# Revit family: Reece_Bath_LAUFEN_Val_Freestanding Bath_1300 mm_Round
name_source: partatom
category: Plumbing Fixtures
revit_build: Autodesk Revit 2018 (Build: 20180329_1100(x64)
units: mm (PartAtom-declared; Revit-internal decimal feet)

## family parameters
Always vertical = Yes
Cut with Voids When Loaded = Yes
Part Type = Normal
Room Calculation Point = Yes
Round Connector Dimension = Use Diameter
Shared = Yes
Work Plane-Based = Yes

## types (1)
- White
    Default Elevation = 0 mm  [stored 0 ft]
    Description = Laufen Val Freestanding Bath with Overflow 1300 Round Sentec White
    Disclaimer = THIS FILE IS THE PROPERTY OF THE REECE GROUP. IT MAY NOT BE REPRODUCED, REVERSE-ENGINEERED OR MODIFIED. ANY REPUBLICATION, TRANSMISSION OR DISTRIBUTION FOR THE PURPOSE OF COMMERCIALLY EXPLOITING THE FILES IS PROHIBITED.
    Keynote = Product #9510105, Reece_Bath_LAUFEN_Val_Freestanding Bath_1300 mm_Round - White
    Manufacturer = Laufen
    Model = Val
    Reece_Bath_Outlet = 40 mm  [stored 0.131234 ft]
    Reece_Detail_Additional = Overflow
    Reece_Detail_Disclaimer = THIS FILE IS THE PROPERTY OF THE REECE GROUP. IT MAY NOT BE REPRODUCED, REVERSE-ENGINEERED OR MODIFIED. ANY REPUBLICATION, TRANSMISSION OR DISTRIBUTION FOR THE PURPOSE OF COMMERCIALLY EXPLOITING THE FILES IS PROHIBITED.
    Reece_Detail_Installation = Freestanding Bath
    Reece_Material_Main = Reece_Acrylic_White
    Reece_Material_Secondary = Reece_Brass_Chrome
    Reece_Overall_Capacity = 460 L
    Reece_Overall_Height = 550 mm
    Reece_Overall_Length = 1300 mm  [stored 4.26509 ft]
    Reece_Overall_Width = 1300 mm  [stored 4.26509 ft]
    Reece_Product_Brand = Laufen
    Reece_Product_Description = LAUFEN Val Freestanding Bath with Overflow 1300 Round Sentec White
    Reece_Product_Mount = Floor Mounted
    Reece_Product_Number = 9510105
    Reece_Product_Sub Brand = Val
    Reece_Product_Type = Bath
    Reece_Product_Web Page = https://www.reece.com.au
    Type Comments = Bath
    URL = https://www.reece.com.au

note: [stored X ft] marks values corroborated as IEEE doubles in the binary element streams (Revit-internal decimal feet)

## geometry (parser evidence)
native form markers: Sweep x3
no freeform markers — native parametric forms only
